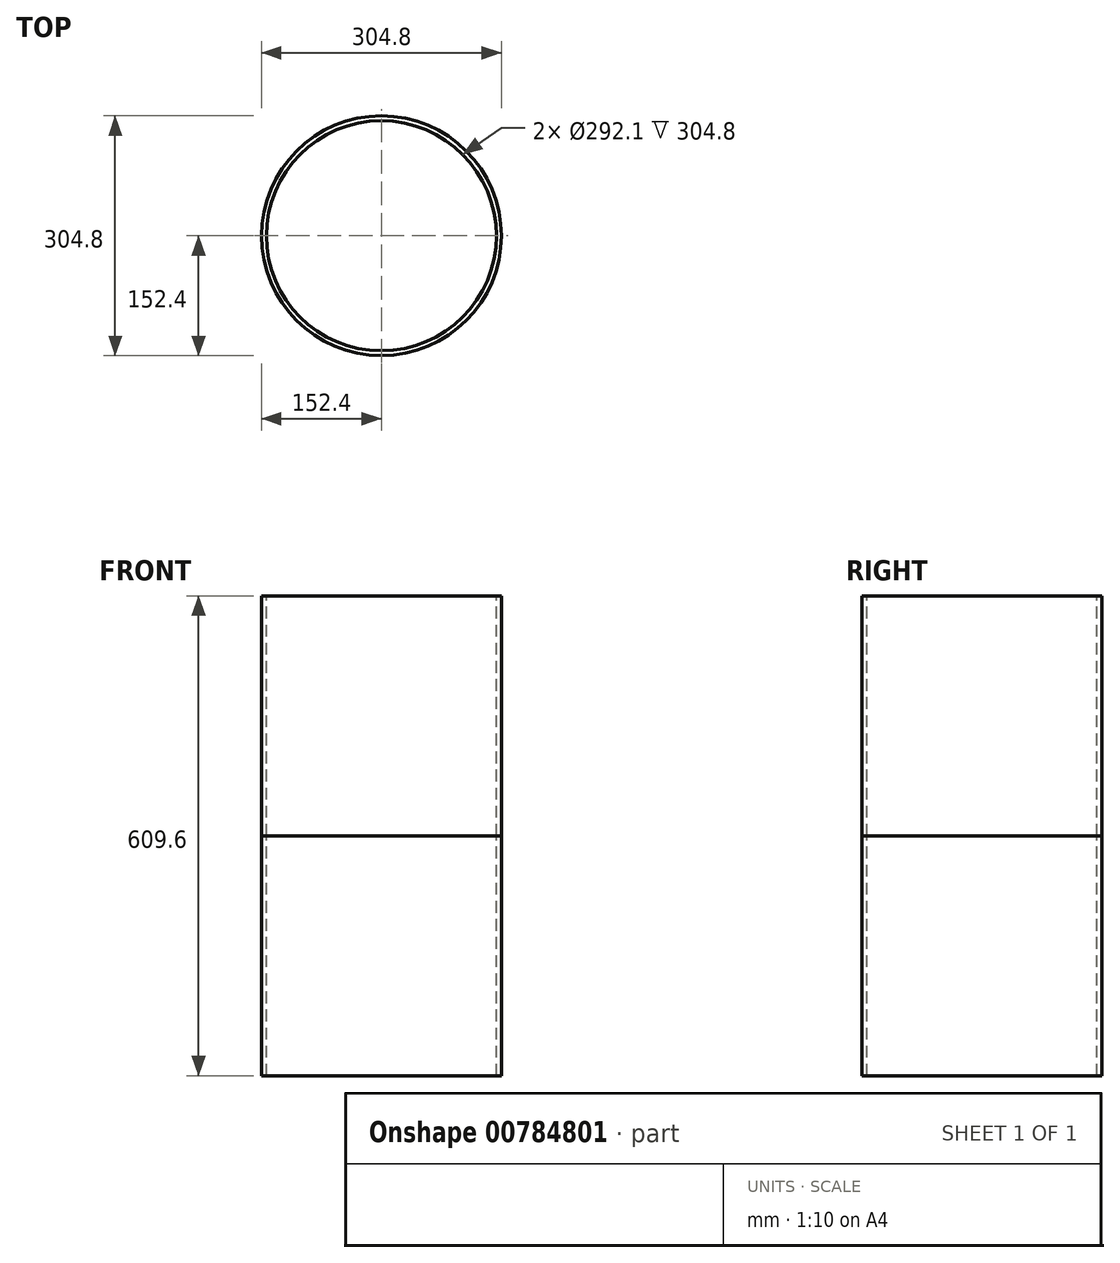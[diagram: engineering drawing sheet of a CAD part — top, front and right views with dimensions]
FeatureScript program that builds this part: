
annotation { "Feature Type Name" : "Feature", "Feature Type Description" : "" }
export const myFeature = defineFeature(function(context is Context, id is Id, definition is map)
    precondition{}
    {
        {
            var Q0;
            Q0=qCreatedBy(makeId("Top.planeOp"),FACE);
            var sketch = newSketch(context, id + "F0", { "sketchPlane" : qUnion([Q0])});
            skCircle(sketch, "E0", {"center": v(0, 0) * mm, "radius": 152.4 * mm});
            skCircle(sketch, "E1", {"center": v(0, 0) * mm, "radius": 146.05 * mm});
            skSolve(sketch);
        }
        {
            var Q0;
            Q0 = qSketchRegion(id + "F0", true);
            extrude(context, id + "F1", {"entities" : qUnion([Q0]), "oppositeDirection" : true, "depth" : 304.8 * mm, "offsetDistance" : 25.4 * mm});
        }
        {
            var Q0;
            Q0=makeQuery(id+"F1.opExtrude","SWEPT_BODY",BODY,{"disambiguationData":[OSD([sQuery(id+"F0.wireOp",EDGE,"E0"),sQuery(id+"F0.wireOp",EDGE,"E1")])]});
            transform(context, id + "F2", {"entities" : qUnion([Q0]), "transformType" : TransformType.TRANSLATION_3D, "dx" : 0 * mm, "dy" : 0 * mm, "dz" : -304.8 * mm, "makeCopy" : true});
        }
    });
